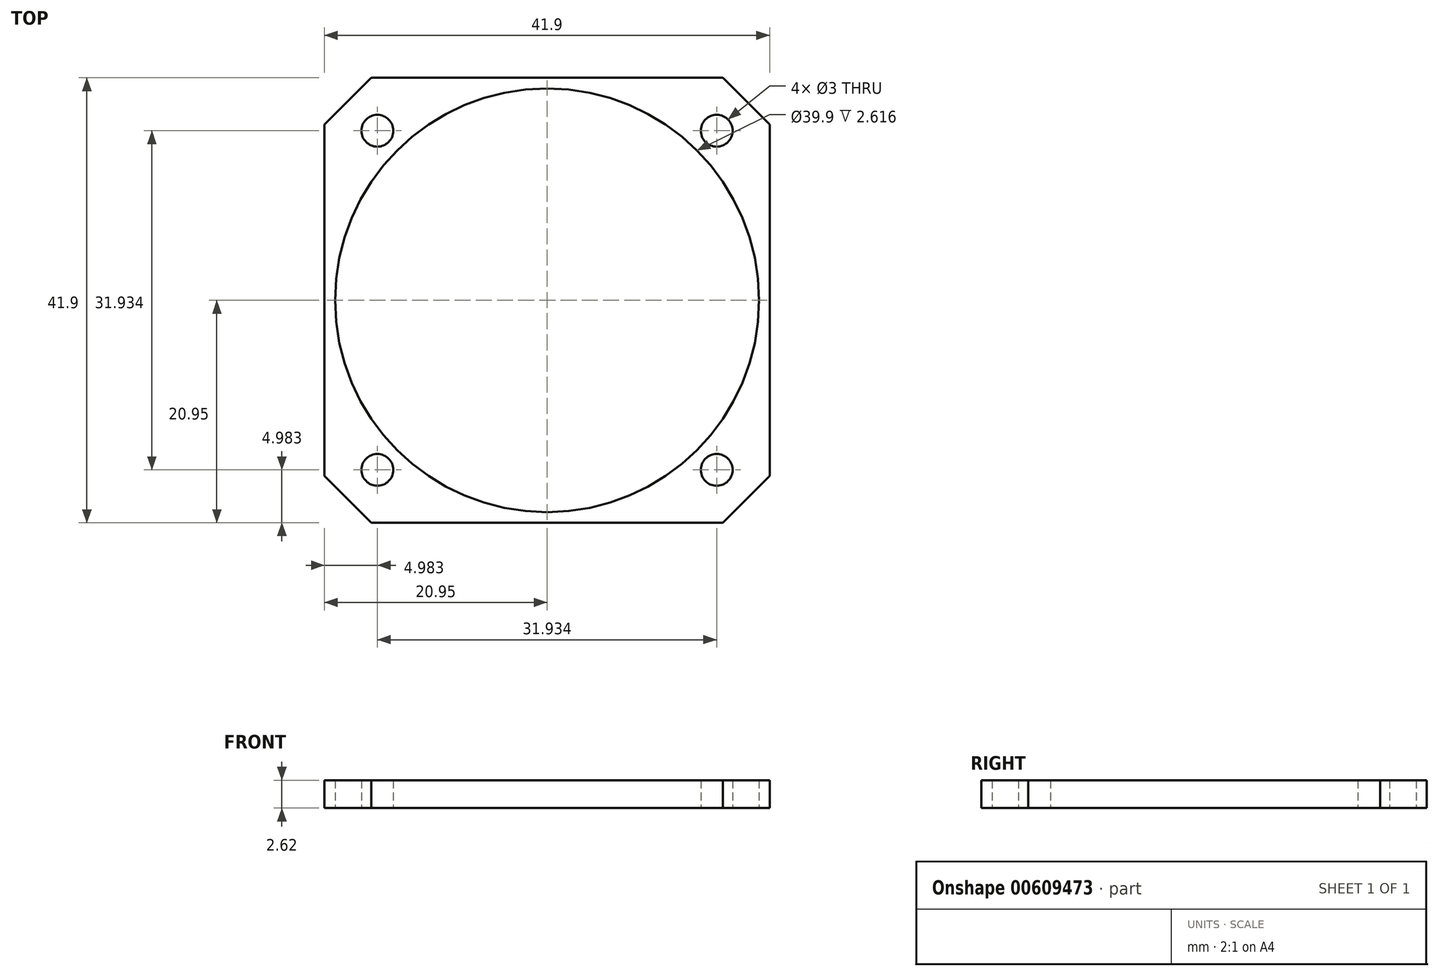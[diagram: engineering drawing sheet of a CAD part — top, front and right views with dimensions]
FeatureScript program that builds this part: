
annotation { "Feature Type Name" : "Feature", "Feature Type Description" : "" }
export const myFeature = defineFeature(function(context is Context, id is Id, definition is map)
    precondition{}
    {
        {
            var Q0;
            Q0=qCreatedBy(makeId("Top.planeOp"),FACE);
            var sketch = newSketch(context, id + "F0", { "sketchPlane" : qUnion([Q0])});
            skCircle(sketch, "E0", {"center": v(0, 0) * mm, "radius": 19.95 * mm});
            skCircle(sketch, "E1", {"center": v(-15.97, 15.97) * mm, "radius": 1.5 * mm});
            skCircle(sketch, "E2.1.0", {"center": v(-15.97, -15.97) * mm, "radius": 1.5 * mm});
            skCircle(sketch, "E2.2.0", {"center": v(15.97, -15.97) * mm, "radius": 1.5 * mm});
            skCircle(sketch, "E2.3.0", {"center": v(15.97, 15.97) * mm, "radius": 1.5 * mm});
            skLineSegment(sketch, "E3.bottom", {"start": v(16.55, -20.95) * mm, "end": v(-16.55, -20.95) * mm});
            skLineSegment(sketch, "E3.top", {"start": v(16.55, 20.95) * mm, "end": v(-16.55, 20.95) * mm});
            skLineSegment(sketch, "E3.left", {"start": v(20.95, -16.55) * mm, "end": v(20.95, 16.55) * mm});
            skLineSegment(sketch, "E3.right", {"start": v(-20.95, -16.55) * mm, "end": v(-20.95, 16.55) * mm});
            skLineSegment(sketch, "E4", {"start": v(-16.55, 20.95) * mm, "end": v(-20.95, 16.55) * mm});
            skPoint(sketch, "E5.orphan", {"position": v(-20.95, 20.95) * mm});
            skLineSegment(sketch, "E6.1.0", {"start": v(-20.95, -16.55) * mm, "end": v(-16.55, -20.95) * mm});
            skLineSegment(sketch, "E6.2.0", {"start": v(16.55, -20.95) * mm, "end": v(20.95, -16.55) * mm});
            skLineSegment(sketch, "E6.3.0", {"start": v(20.95, 16.55) * mm, "end": v(16.55, 20.95) * mm});
            skPoint(sketch, "E7.orphan", {"position": v(20.95, 20.95) * mm});
            skPoint(sketch, "E8.orphan", {"position": v(20.95, -20.95) * mm});
            skPoint(sketch, "E9.orphan", {"position": v(-20.95, -20.95) * mm});
            skSolve(sketch);
        }
        {
            var Q0;
            Q0 = qSketchRegion(id + "F0", true);
            extrude(context, id + "F1", {"entities" : qUnion([Q0]), "depth" : 2.62 * mm, "offsetDistance" : 25.4 * mm});
        }
        {
            var Q0;
            Q0=makeQuery(id+"F1.opExtrude","CAP_EDGE",EDGE,{"disambiguationData":[OSD([sQuery(id+"F0.wireOp",EDGE,"E3.left")])],"isStart":false});
            var Q1;
            Q1=qCreatedBy(makeId("Top.planeOp"),FACE);
            cPlane(context, id + "F2", {"entities" : qUnion([Q0, Q1]), "cplaneType" : CPlaneType.LINE_ANGLE, "offset" : 25.4 * mm, "angle" : 30 * degree, "width" : 152.4 * mm, "height" : 152.4 * mm});
        }
        {
            var Q0;
            Q0=qCreatedBy(id+"F2.planeOp",FACE);
            cPlane(context, id + "F3", {"entities" : qUnion([Q0]), "cplaneType" : CPlaneType.OFFSET, "offset" : 25.4 * mm, "oppositeDirection" : true, "width" : 152.4 * mm, "height" : 152.4 * mm});
        }
        {
            var Q0;
            Q0=qCreatedBy(id+"F3.planeOp",FACE);
            var sketch = newSketch(context, id + "F4", { "sketchPlane" : qUnion([Q0])});
            skArc(sketch, "E10", {"start": v(-56.45, -12.7) * mm, "mid": v(-43.75, 0) * mm, "end": v(-56.45, 12.7) * mm});
            skArc(sketch, "E11", {"start": v(-56.45, -25.4) * mm, "mid": v(-31.05, 0) * mm, "end": v(-56.45, 25.4) * mm});
            skArc(sketch, "E12", {"start": v(-56.45, 25.4) * mm, "mid": v(-62.8, 19.05) * mm, "end": v(-56.45, 12.7) * mm});
            skArc(sketch, "E13.MirrorC", {"start": v(-56.45, -25.4) * mm, "mid": v(-62.8, -19.05) * mm, "end": v(-56.45, -12.7) * mm});
            skSolve(sketch);
        }
    });
